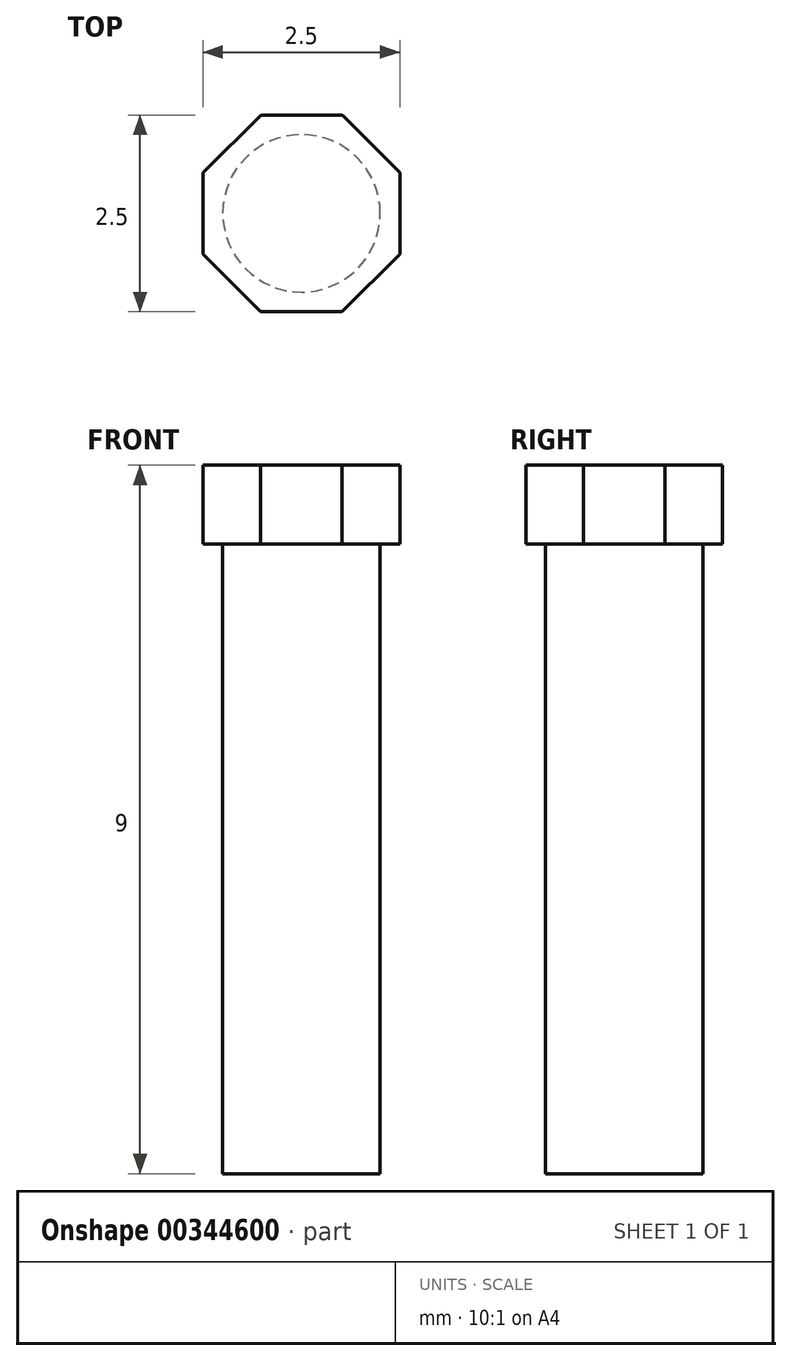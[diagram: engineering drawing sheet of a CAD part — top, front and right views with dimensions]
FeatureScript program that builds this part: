
annotation { "Feature Type Name" : "Feature", "Feature Type Description" : "" }
export const myFeature = defineFeature(function(context is Context, id is Id, definition is map)
    precondition{}
    {
        {
            var Q0;
            Q0=qCreatedBy(makeId("Top.planeOp"),FACE);
            var sketch = newSketch(context, id + "F0", { "sketchPlane" : qUnion([Q0])});
            skLineSegment(sketch, "E0", {"start": v(0, 0) * mm, "end": v(0, 1.25) * mm});
            skLineSegment(sketch, "E1", {"start": v(0, 0) * mm, "end": v(0, -1.25) * mm});
            skLineSegment(sketch, "E2", {"start": v(0, 0) * mm, "end": v(1.25, 0) * mm});
            skLineSegment(sketch, "E3", {"start": v(0, 0) * mm, "end": v(-1.25, 0) * mm});
            skLineSegment(sketch, "E4", {"start": v(-1.25, 0) * mm, "end": v(-1.25, -0.52) * mm});
            skLineSegment(sketch, "E5", {"start": v(-1.25, -0.52) * mm, "end": v(-1.25, 0.52) * mm});
            skLineSegment(sketch, "E6.bottom", {"start": v(-0.52, 1.25) * mm, "end": v(0.52, 1.25) * mm});
            skLineSegment(sketch, "E6.top", {"start": v(-0.52, -1.25) * mm, "end": v(0.52, -1.25) * mm});
            skLineSegment(sketch, "E6.left", {"start": v(-1.25, 0.52) * mm, "end": v(-1.25, -0.52) * mm});
            skLineSegment(sketch, "E6.right", {"start": v(1.25, 0.52) * mm, "end": v(1.25, -0.52) * mm});
            skLineSegment(sketch, "E7", {"start": v(0, 0) * mm, "end": v(0.89, 0.88) * mm});
            skLineSegment(sketch, "E8", {"start": v(0, 0) * mm, "end": v(-0.89, -0.88) * mm});
            skLineSegment(sketch, "E9", {"start": v(0, 0) * mm, "end": v(0.88, -0.89) * mm});
            skLineSegment(sketch, "E10", {"start": v(0, 0) * mm, "end": v(-0.88, 0.89) * mm});
            skLineSegment(sketch, "E11", {"start": v(-0.88, 0.89) * mm, "end": v(-1.25, 0.52) * mm});
            skLineSegment(sketch, "E12", {"start": v(-1.25, 0.52) * mm, "end": v(-0.52, 1.25) * mm});
            skLineSegment(sketch, "E13.bottom", {"start": v(0.52, 1.25) * mm, "end": v(1.25, 0.52) * mm});
            skLineSegment(sketch, "E13.top", {"start": v(-1.25, -0.52) * mm, "end": v(-0.52, -1.25) * mm});
            skLineSegment(sketch, "E13.left", {"start": v(-0.52, 1.25) * mm, "end": v(-1.25, 0.52) * mm});
            skLineSegment(sketch, "E13.right", {"start": v(1.25, -0.52) * mm, "end": v(0.52, -1.25) * mm});
            skLineSegment(sketch, "E14.0", {"start": v(-0.89, -0.88) * mm, "end": v(-0.52, -1.25) * mm, "construction": true});
            skLineSegment(sketch, "E15.0", {"start": v(0.52, -1.25) * mm, "end": v(0.88, -0.89) * mm, "construction": true});
            skSolve(sketch);
        }
        {
            var Q0;
            Q0=qSketchRegion(id+"F0",true);
            extrude(context, id + "F1", {"entities" : qUnion([Q0]), "depth" : 1 * mm});
        }
        {
            var Q0;
            Q0=makeQuery(id+"F1.opExtrude","CAP_FACE",FACE,{"disambiguationData":[OSD([sQuery(id+"F0.wireOp",EDGE,"E6.bottom"),sQuery(id+"F0.wireOp",EDGE,"E6.top"),sQuery(id+"F0.wireOp",EDGE,"E6.left"),sQuery(id+"F0.wireOp",EDGE,"E6.right"),sQuery(id+"F0.wireOp",EDGE,"E13.bottom"),sQuery(id+"F0.wireOp",EDGE,"E13.top"),sQuery(id+"F0.wireOp",EDGE,"E13.left"),sQuery(id+"F0.wireOp",EDGE,"E13.right")])],"isStart":false});
            var sketch = newSketch(context, id + "F2", { "sketchPlane" : qUnion([Q0])});
            skCircle(sketch, "E16", {"center": v(0, 0) * mm, "radius": 1 * mm});
            skSolve(sketch);
        }
        {
            var Q0;
            Q0=qSketchRegion(id+"F2",true);
            extrude(context, id + "F3", {"entities" : qUnion([Q0]), "operationType" : NewBodyOperationType.ADD, "oppositeDirection" : true, "depth" : 9 * mm});
        }
    });
